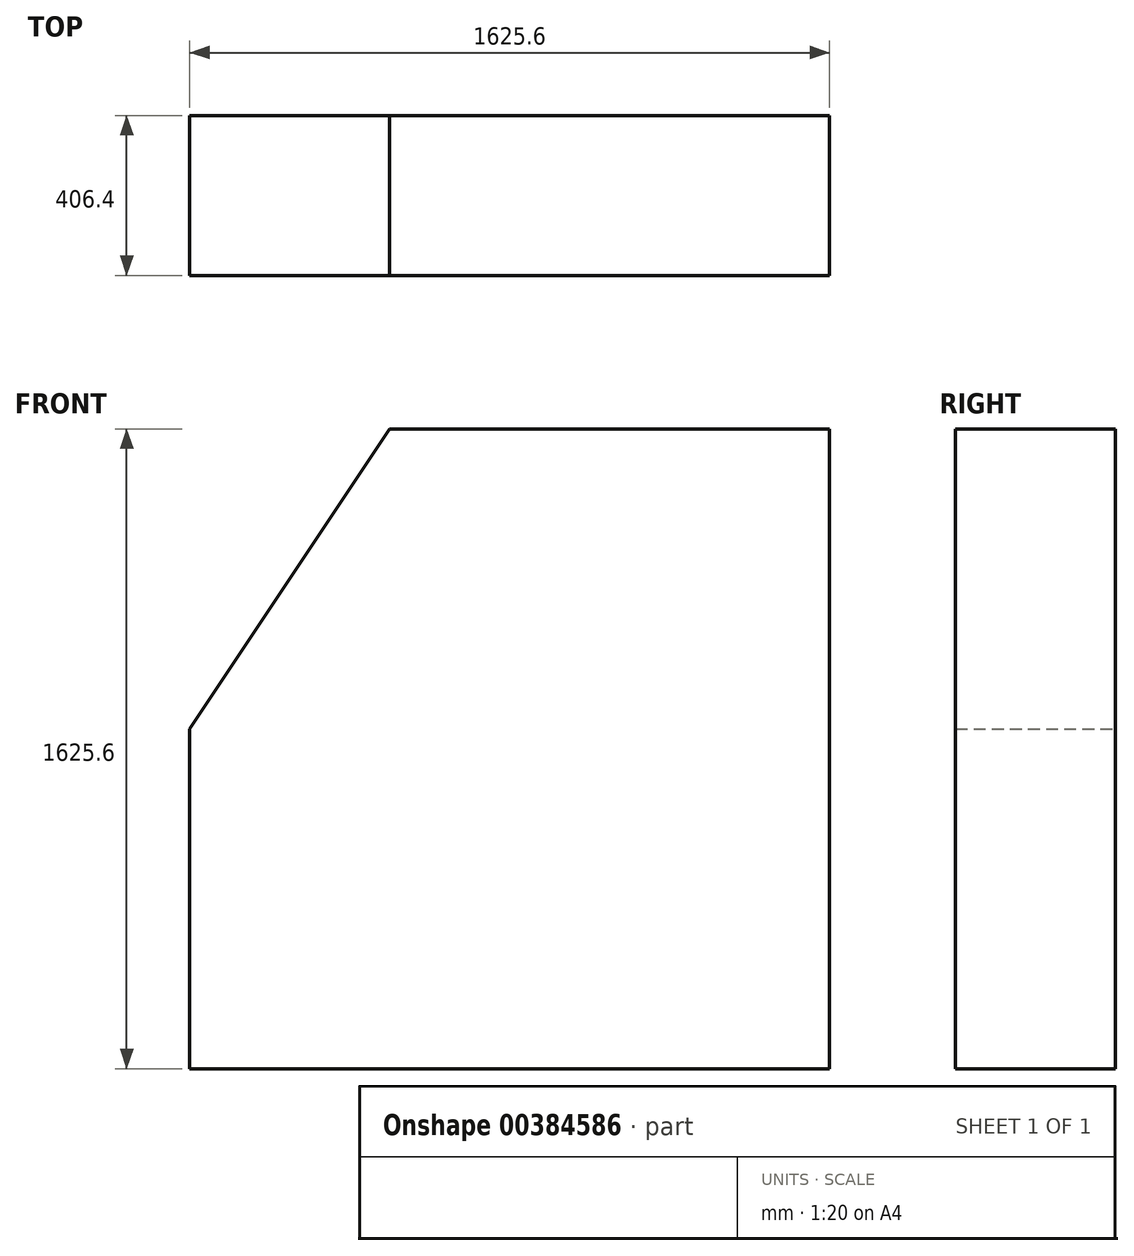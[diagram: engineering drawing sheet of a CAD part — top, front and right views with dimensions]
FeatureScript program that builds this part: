
annotation { "Feature Type Name" : "Feature", "Feature Type Description" : "" }
export const myFeature = defineFeature(function(context is Context, id is Id, definition is map)
    precondition{}
    {
        {
            var Q0;
            Q0=qCreatedBy(makeId("Front.planeOp"),FACE);
            var sketch = newSketch(context, id + "F0", { "sketchPlane" : qUnion([Q0])});
            skLineSegment(sketch, "E0", {"start": v(0, 0) * mm, "end": v(1625.6, 0) * mm});
            skLineSegment(sketch, "E1", {"start": v(1625.6, 0) * mm, "end": v(1625.6, 1625.6) * mm});
            skLineSegment(sketch, "E2", {"start": v(1625.6, 1625.6) * mm, "end": v(508, 1625.6) * mm});
            skLineSegment(sketch, "E3", {"start": v(0, 0) * mm, "end": v(0, 863.6) * mm});
            skLineSegment(sketch, "E4", {"start": v(0, 863.6) * mm, "end": v(508, 1625.6) * mm});
            skSolve(sketch);
        }
        {
            var Q0;
            Q0 = qSketchRegion(id + "F0", true);
            extrude(context, id + "F1", {"entities" : qUnion([Q0]), "depth" : 406.4 * mm});
        }
    });
